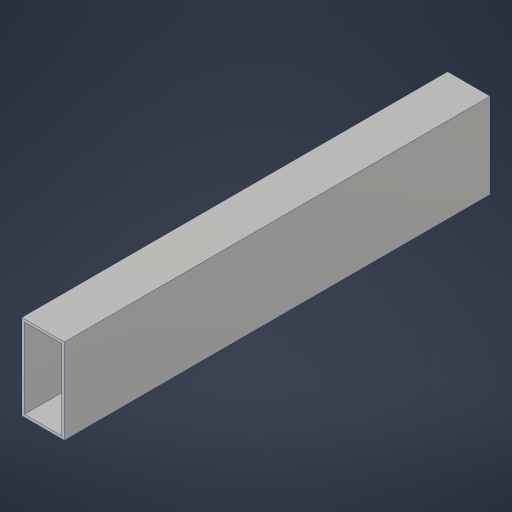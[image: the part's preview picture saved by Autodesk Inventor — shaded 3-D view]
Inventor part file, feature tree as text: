
AUTODESK INVENTOR PART (.ipt)
format: ipt  version: 2023.4 (Build 274418000, 418)  size: 161,280 bytes
history: native  units: in
note: dims shown in document units (in); Inventor stores cm internally (conversion verified against a paired STEP export)
features: extrude x1
ambient origin geometry x8: Origin, YZ Plane, XZ Plane, XY Plane, X Axis, Y Axis, Z Axis, Center Point
bodies: Solid1 (feature_tree)
feature tree (1):
  extrude  "Extrusion1"  TaperAngle=0.0deg  [1 undecoded]
note: 1 required parameter value undecoded (feature->parameter linkage not recoverable at this tier; creation-order binding heuristic only, values carry confidence <= 0.55)
